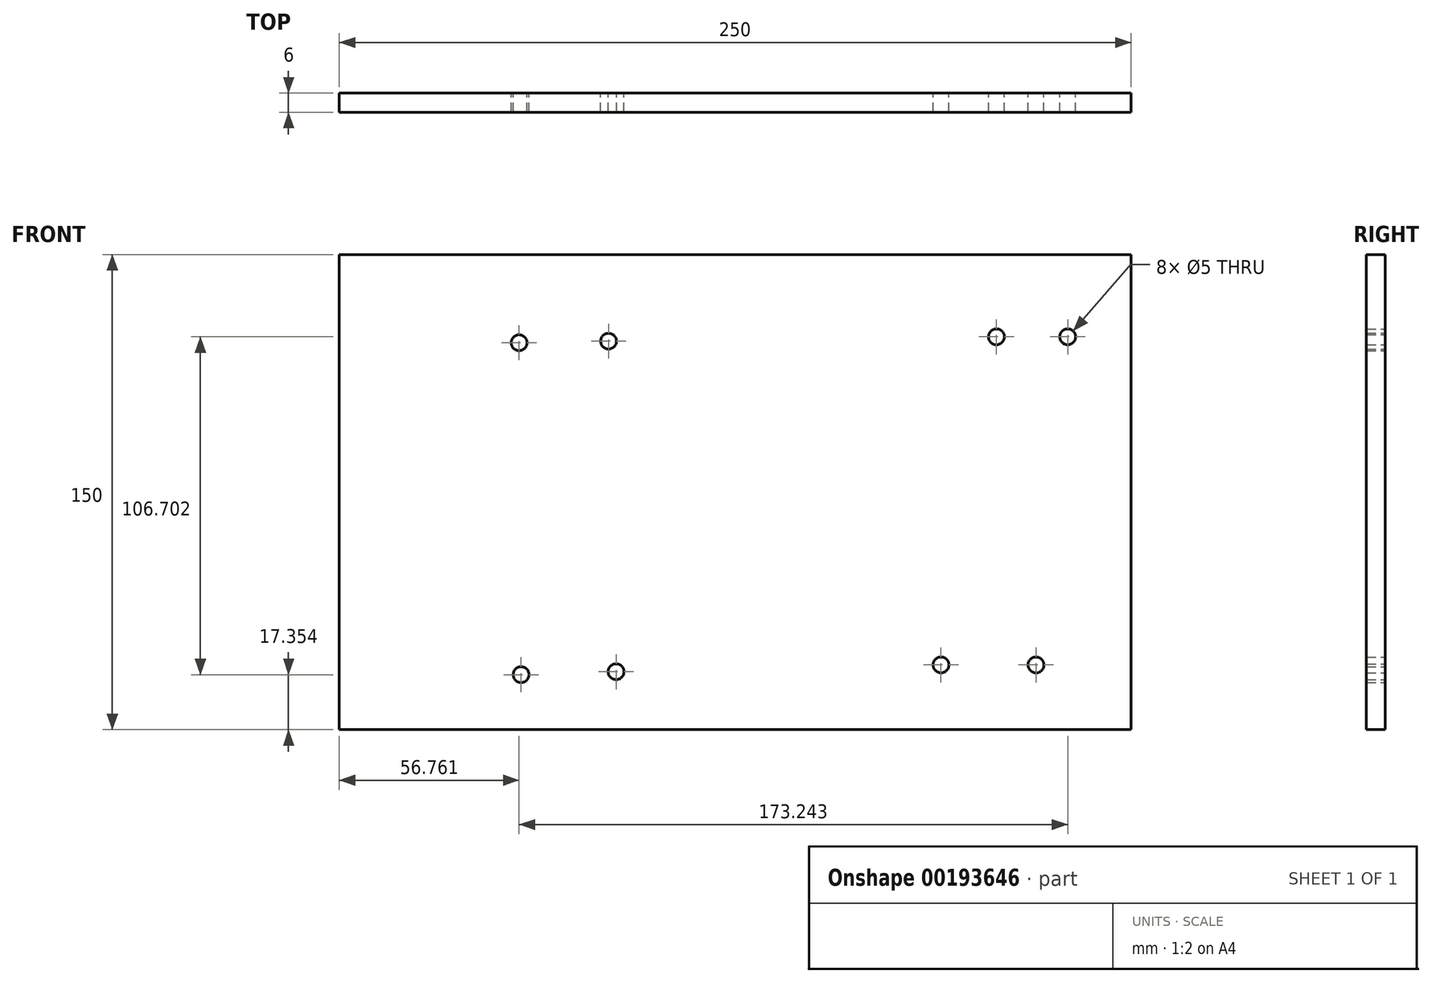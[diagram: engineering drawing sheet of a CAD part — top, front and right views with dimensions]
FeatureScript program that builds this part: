
annotation { "Feature Type Name" : "Feature", "Feature Type Description" : "" }
export const myFeature = defineFeature(function(context is Context, id is Id, definition is map)
    precondition{}
    {
        {
            var Q0;
            Q0=qCreatedBy(makeId("Front.planeOp"),FACE);
            var sketch = newSketch(context, id + "F0", { "sketchPlane" : qUnion([Q0])});
            skLineSegment(sketch, "E0.bottom", {"start": v(105.86, -73.78) * mm, "end": v(-144.14, -73.78) * mm});
            skLineSegment(sketch, "E0.top", {"start": v(105.86, 76.22) * mm, "end": v(-144.14, 76.22) * mm});
            skLineSegment(sketch, "E0.left", {"start": v(105.86, -73.78) * mm, "end": v(105.86, 76.22) * mm});
            skLineSegment(sketch, "E0.right", {"start": v(-144.14, -73.78) * mm, "end": v(-144.14, 76.22) * mm});
            skCircle(sketch, "E1", {"center": v(75.86, -53.35) * mm, "radius": 2.5 * mm});
            skCircle(sketch, "E2", {"center": v(45.86, -53.35) * mm, "radius": 2.5 * mm});
            skCircle(sketch, "E3", {"center": v(-56.75, -55.5) * mm, "radius": 2.5 * mm});
            skCircle(sketch, "E4", {"center": v(-86.75, -56.43) * mm, "radius": 2.5 * mm});
            skCircle(sketch, "E5", {"center": v(85.86, 50.28) * mm, "radius": 2.5 * mm});
            skCircle(sketch, "E6", {"center": v(63.36, 50.28) * mm, "radius": 2.5 * mm});
            skCircle(sketch, "E7", {"center": v(-59.13, 48.9) * mm, "radius": 2.5 * mm});
            skCircle(sketch, "E8", {"center": v(-87.38, 48.4) * mm, "radius": 2.5 * mm});
            skSolve(sketch);
        }
        {
            var Q0;
            Q0=makeQuery(id+"F0.imprint","IMPRINT",FACE,{"disambiguationData":[TD([[makeQuery(id+"F0.imprint","IMPRINT",EDGE,{"derivedFrom":sQuery(id+"F0.wireOp",EDGE,"E0.bottom")}),-1.0]])]});
            extrude(context, id + "F1", {"entities" : qUnion([Q0]), "depth" : 6 * mm});
        }
    });
